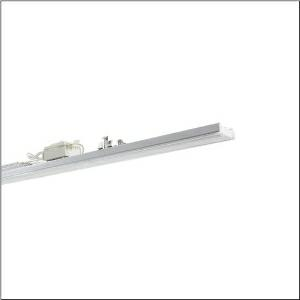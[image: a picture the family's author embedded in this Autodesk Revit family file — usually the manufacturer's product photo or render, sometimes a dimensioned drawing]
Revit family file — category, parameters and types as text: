
# Revit family: licross_r__11_recessed_ho_51tl1ecn4cxs_7d08
name_source: partatom
category: Lighting Fixtures
units: mm (PartAtom-declared; Revit-internal decimal feet)

## family parameters
Cut with Voids When Loaded = No
Host = Face
Light Source = No
Part Type = Normal
Room Calculation Point = No
Round Connector Dimension = Use Diameter
Shared = No

## types (1)
- --- (1 x LED, 12420 lm, 66.5 W, 4000K)
    Apparent Load = 67 VA
    CIE Flux Codes = 85 95 99 100 100
    Color Rendering = 80
    Color Temperature = 4000K
    Default Elevation = 1800 mm
    Description = Licross® 11 Recessed HO, luminaire insert, of sheet steel, coil coated, white, length: 1.500mm, width: 66mm, height: 67mm, LED rated luminous flux: 12.420lm, light colour: 840, control gear: ON/OFF Multilumen, CLOi, with plug, 3-pole, with phase selection, mains connection: 220..240V, AC, 50/60Hz, start of lifetime: 67W, end of service life: 75W, halogen-free wiring, primary light control with lens, of plastic, primary optical cover: cover, of PMMA, light emission: direct distribution, primary light characteristic: symmetric, protection rating (complete): IP40, insulation class (complete): insulation class I (protective earthing), certification: CE, ENEC, VDE, UKCA, protection symbol: D if used in an environment without relevant dust loads with corresponding accessories, impact resistance: IK06, permissible ambient temperature for indoor applications: -35..+35°C, corresponds to IFS (International Featured Standards) requirements for safety and quality in the food industry, reducing of maximum allowable ambient temperature of 5°C with ceiling mounting, LABS conformity tested according to VDMA 24364:2018-05, packaging unit: 1 piece
    Height = 58 mm
    Lamp = 1 x LED
    Lamp Light Flux = 12420 lm
    Lamp Power = 66.5 W
    Lamp count = 1
    Length = 1500 mm
    Luminous efficacy = 187 lm/W
    Manufacturer = Siteco
    ModVariant = No
    Model = 51TL1ECN4CXS
    Mounting Place = Ceiling
    Mounting Type = Pendant
    Number of Poles = 1
    OnlyDefault = Yes
    Power Factor = 1
    Product Name = Licross® 11 Recessed HO
    Product group = luminaire insert
    ProductGroupID = 902
    Protection Class = Protection class I
    Protection Degree = IP 40
    RLX_Detail_Level = 1
    RLX_Emergency_Light_Flux = 0 lm
    RLX_Emergency_Type = 0
    RLX_Emergency_Type_DB = No
    RlxData = <blob elided: 22373 chars, md5=4204db87>
    Socket = socket
    Standby Power = 0 W
    System Light Flux = 12420 lm
    System Power = 67 W
    Type Comments = factory setting: luminous flux: 100 % | (A | C | E) | 156 mA
    Type Image = l_1296930.jpg
    URL = http://relux.com
    VarID = @adj_084226
    Voltage = 0 V
    Weight = 0.00 kg
    Width = 66 mm

## geometry (parser evidence)
native form markers: Blend x4, Sweep x10
no freeform markers — native parametric forms only
